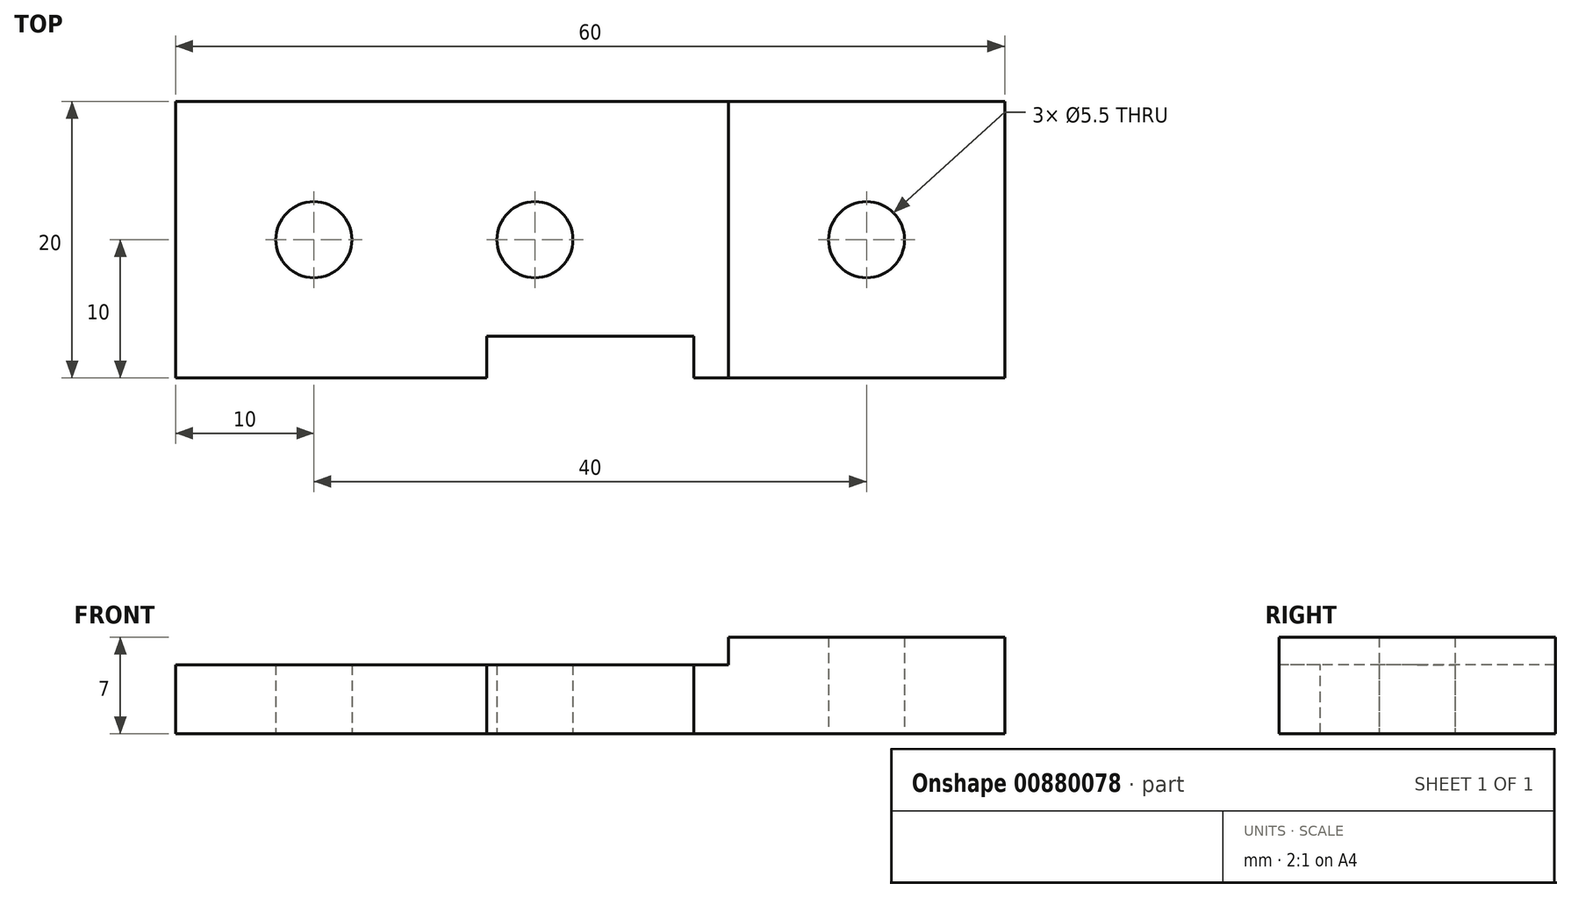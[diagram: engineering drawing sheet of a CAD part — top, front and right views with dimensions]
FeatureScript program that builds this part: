
annotation { "Feature Type Name" : "Feature", "Feature Type Description" : "" }
export const myFeature = defineFeature(function(context is Context, id is Id, definition is map)
    precondition{}
    {
        {
            var Q0;
            Q0=qCreatedBy(makeId("Top.planeOp"),FACE);
            var sketch = newSketch(context, id + "F0", { "sketchPlane" : qUnion([Q0])});
            skLineSegment(sketch, "E0.bottom", {"start": v(-30, 10) * mm, "end": v(30, 10) * mm});
            skLineSegment(sketch, "E0.top", {"start": v(-30, -10) * mm, "end": v(30, -10) * mm});
            skLineSegment(sketch, "E0.left", {"start": v(-30, 10) * mm, "end": v(-30, -10) * mm});
            skLineSegment(sketch, "E0.right", {"start": v(30, 10) * mm, "end": v(30, -10) * mm});
            skPoint(sketch, "E0.middle", {"position": v(0, 0) * mm});
            skLineSegment(sketch, "E1", {"start": v(-30, 0) * mm, "end": v(30, 0) * mm, "construction": true});
            skLineSegment(sketch, "E2", {"start": v(0, 10) * mm, "end": v(0, -10) * mm, "construction": true});
            skLineSegment(sketch, "E3", {"start": v(-20, 10) * mm, "end": v(-20, -10) * mm, "construction": true});
            skLineSegment(sketch, "E4", {"start": v(20, 10) * mm, "end": v(20, -10) * mm, "construction": true});
            skPoint(sketch, "E5", {"position": v(-20, 0) * mm});
            skPoint(sketch, "E6", {"position": v(20, 0) * mm});
            skLineSegment(sketch, "E7", {"start": v(10, 10) * mm, "end": v(10, -10) * mm});
            skPoint(sketch, "E8", {"position": v(-4, 0) * mm});
            skLineSegment(sketch, "E9.bottom", {"start": v(7.5, -7) * mm, "end": v(-7.5, -7) * mm});
            skLineSegment(sketch, "E9.top", {"start": v(7.5, -13) * mm, "end": v(-7.5, -13) * mm});
            skLineSegment(sketch, "E9.left", {"start": v(7.5, -7) * mm, "end": v(7.5, -13) * mm});
            skLineSegment(sketch, "E9.right", {"start": v(-7.5, -7) * mm, "end": v(-7.5, -13) * mm});
            skPoint(sketch, "E9.middle", {"position": v(0, -10) * mm});
            skSolve(sketch);
        }
        {
            var Q0;
            Q0=makeQuery(id+"F0.imprint","IMPRINT",FACE,{"disambiguationData":[TD([[makeQuery(id+"F0.imprint","IMPRINT",EDGE,{"derivedFrom":sQuery(id+"F0.wireOp",EDGE,"E0.bottom")}),-1.0]])]});
            var Q1;
            {var subQ0=sQuery(id+"F0.wireOp",EDGE,"E0.left");Q1=makeQuery(id+"F0.imprint","IMPRINT",FACE,{"disambiguationData":[TD([[makeQuery(id+"F0.imprint","IMPRINT",EDGE,{"derivedFrom":subQ0}),1.0]])]});}
            extrude(context, id + "F1", {"entities" : qUnion([Q0, Q1]), "oppositeDirection" : true, "depth" : 5 * mm, "offsetDistance" : 25 * mm});
        }
        {
            var Q0;
            {var subQ0=sQuery(id+"F0.wireOp",EDGE,"E0.right");Q0=makeQuery(id+"F0.imprint","IMPRINT",FACE,{"disambiguationData":[TD([[makeQuery(id+"F0.imprint","IMPRINT",EDGE,{"derivedFrom":subQ0}),-1.0]])]});}
            extrude(context, id + "F2", {"entities" : qUnion([Q0]), "operationType" : NewBodyOperationType.ADD, "depth" : 2 * mm, "offsetDistance" : 25 * mm});
        }
        {
            var Q0;
            Q0=makeQuery(id+"F1.opExtrude","CAP_FACE",FACE,{"disambiguationData":[OSD([sQuery(id+"F0.wireOp",EDGE,"E0.bottom"),sQuery(id+"F0.wireOp",EDGE,"E0.top"),sQuery(id+"F0.wireOp",EDGE,"E0.left"),sQuery(id+"F0.wireOp",EDGE,"E0.right")])],"isStart":false});
            var sketch = newSketch(context, id + "F3", { "sketchPlane" : qUnion([Q0])});
            skPoint(sketch, "E10.0", {"position": v(-20, 0) * mm});
            skPoint(sketch, "E10.2", {"position": v(20, 0) * mm});
            skPoint(sketch, "E11.0", {"position": v(-4, 0) * mm});
            skSolve(sketch);
        }
        {
            var Q0;
            Q0=sQuery(id+"F3.wireOp",VERTEX,"E10.0");
            var Q1;
            Q1=sQuery(id+"F3.wireOp",VERTEX,"E10.2");
            var Q2;
            Q2=sQuery(id+"F3.wireOp",VERTEX,"E11.0");
            var Q3;
            Q3=makeQuery(id+"F1.opExtrude","SWEPT_BODY",BODY,{"disambiguationData":[OSD([sQuery(id+"F0.wireOp",EDGE,"E0.bottom"),sQuery(id+"F0.wireOp",EDGE,"E0.top"),sQuery(id+"F0.wireOp",EDGE,"E0.left"),sQuery(id+"F0.wireOp",EDGE,"E0.right")])]});
            hole(context, id + "F4", {"style" : HoleStyle.SIMPLE, "endStyle" : HoleEndStyle.THROUGH, "standardTappedOrClearance" : lookupTablePath({ "fit" : "Normal", "standard" : "ISO", "size" : "M5", "type" : "Clearance" }), "standardBlindInLast" : lookupTablePath({ "fit" : "Normal", "standard" : "ISO", "size" : "M5", "type" : "Clearance" }), "holeDiameter" : 5.5 * mm, "majorDiameter" : 5 * mm, "isTappedThrough" : true, "tappedDepth" : 3.95 * mm, "tapClearance" : 3, "locations" : qUnion([Q0, Q1, Q2]), "scope" : qUnion([Q3])});
        }
    });
